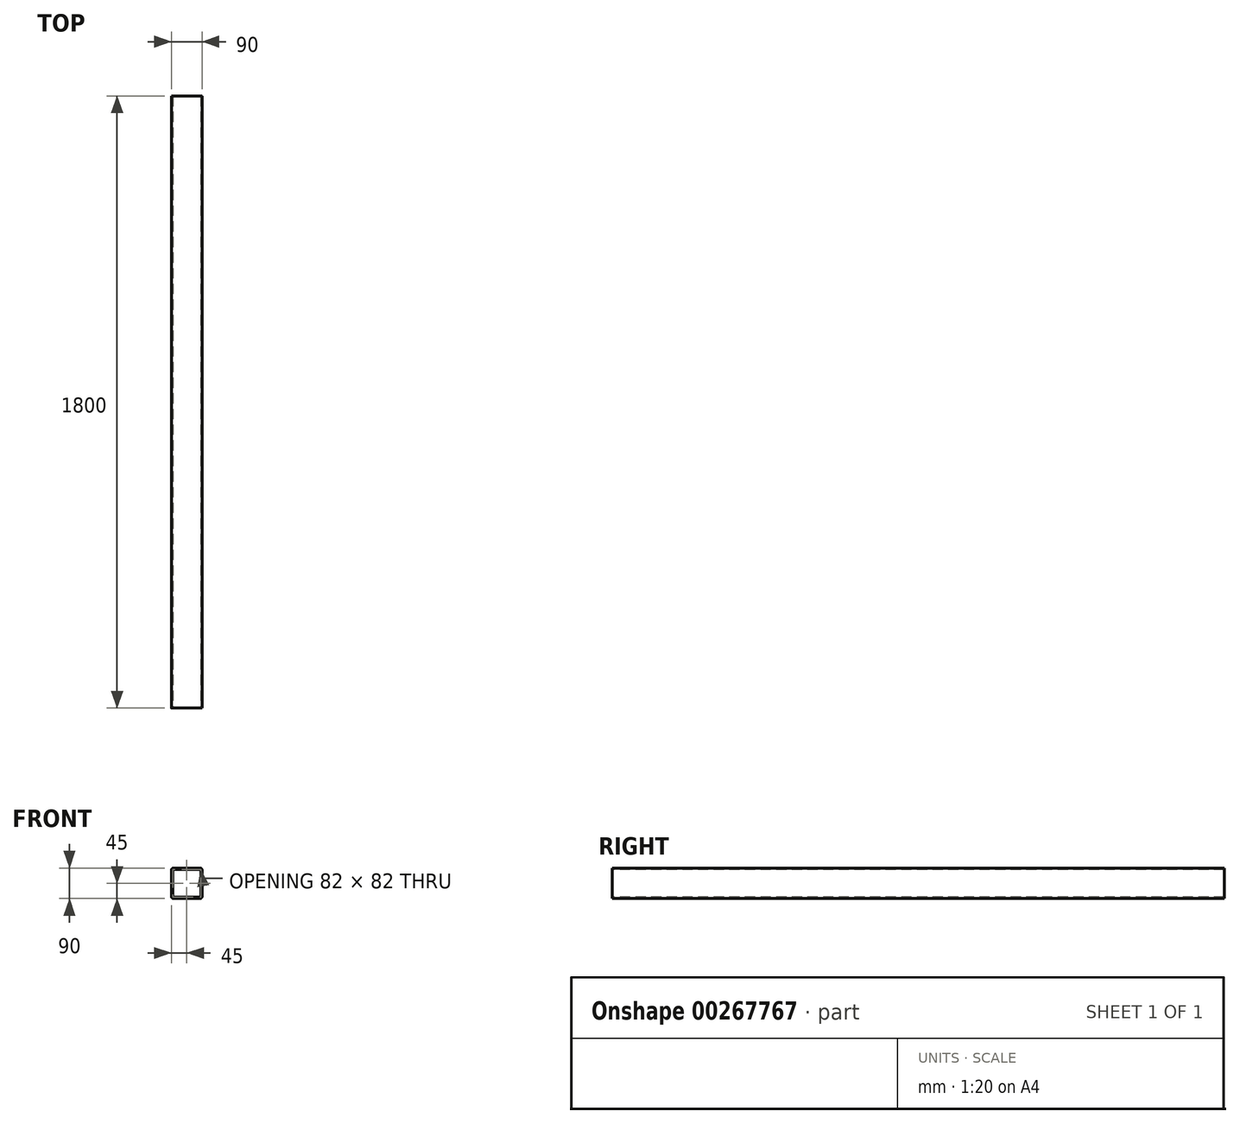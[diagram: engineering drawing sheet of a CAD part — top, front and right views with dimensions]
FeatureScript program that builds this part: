
annotation { "Feature Type Name" : "Feature", "Feature Type Description" : "" }
export const myFeature = defineFeature(function(context is Context, id is Id, definition is map)
    precondition{}
    {
        {
            var Q0;
            Q0=qCreatedBy(makeId("Front.planeOp"),FACE);
            var sketch = newSketch(context, id + "F0", { "sketchPlane" : qUnion([Q0])});
            skLineSegment(sketch, "E0.bottom", {"start": v(39, 45) * mm, "end": v(-39, 45) * mm});
            skLineSegment(sketch, "E0.top", {"start": v(39, -45) * mm, "end": v(-39, -45) * mm});
            skLineSegment(sketch, "E0.left", {"start": v(45, 39) * mm, "end": v(45, -39) * mm});
            skLineSegment(sketch, "E0.right", {"start": v(-45, 39) * mm, "end": v(-45, -39) * mm});
            skPoint(sketch, "E0.middle", {"position": v(0, 0) * mm});
            skPoint(sketch, "E1.visualSharp", {"position": v(-45, 45) * mm});
            skArc(sketch, "E1.filletArc", {"start": v(-39, 45) * mm, "mid": v(-43.24, 43.24) * mm, "end": v(-45, 39) * mm});
            skPoint(sketch, "E2.visualSharp", {"position": v(45, 45) * mm});
            skArc(sketch, "E2.filletArc", {"start": v(45, 39) * mm, "mid": v(43.24, 43.24) * mm, "end": v(39, 45) * mm});
            skPoint(sketch, "E3.visualSharp", {"position": v(45, -45) * mm});
            skArc(sketch, "E3.filletArc", {"start": v(39, -45) * mm, "mid": v(43.24, -43.24) * mm, "end": v(45, -39) * mm});
            skPoint(sketch, "E4.visualSharp", {"position": v(-45, -45) * mm});
            skArc(sketch, "E4.filletArc", {"start": v(-45, -39) * mm, "mid": v(-43.24, -43.24) * mm, "end": v(-39, -45) * mm});
            skArc(sketch, "E5.0", {"start": v(-39, 41) * mm, "mid": v(-40.41, 40.41) * mm, "end": v(-41, 39) * mm});
            skLineSegment(sketch, "E5.1", {"start": v(39, 41) * mm, "end": v(-39, 41) * mm});
            skLineSegment(sketch, "E5.2", {"start": v(-41, 39) * mm, "end": v(-41, -39) * mm});
            skArc(sketch, "E5.3", {"start": v(41, 39) * mm, "mid": v(40.41, 40.41) * mm, "end": v(39, 41) * mm});
            skArc(sketch, "E5.4", {"start": v(-41, -39) * mm, "mid": v(-40.41, -40.41) * mm, "end": v(-39, -41) * mm});
            skLineSegment(sketch, "E5.5", {"start": v(39, -41) * mm, "end": v(-39, -41) * mm});
            skArc(sketch, "E5.6", {"start": v(39, -41) * mm, "mid": v(40.41, -40.41) * mm, "end": v(41, -39) * mm});
            skLineSegment(sketch, "E5.7", {"start": v(41, 39) * mm, "end": v(41, -39) * mm});
            skSolve(sketch);
        }
        {
            var Q0;
            Q0=makeQuery(id+"F0.imprint","IMPRINT",FACE,{"disambiguationData":[TD([[makeQuery(id+"F0.imprint","IMPRINT",EDGE,{"derivedFrom":sQuery(id+"F0.wireOp",EDGE,"E0.bottom")}),1.0]])]});
            extrude(context, id + "F1", {"entities" : qUnion([Q0]), "oppositeDirection" : true, "depth" : 1800 * mm});
        }
    });
